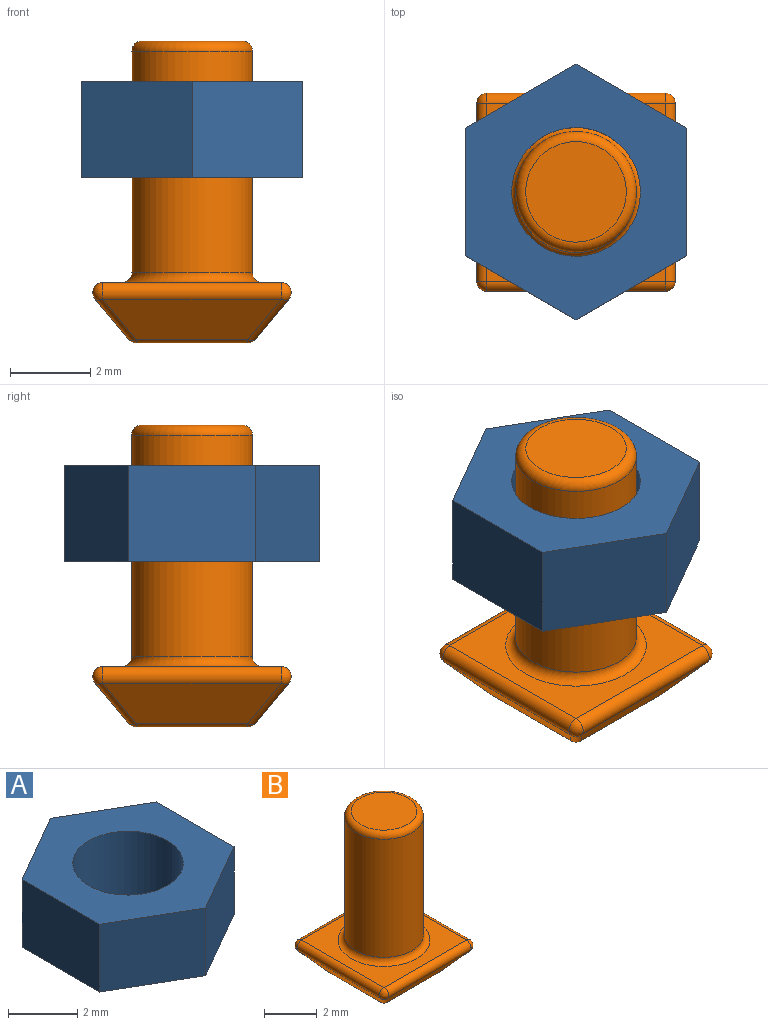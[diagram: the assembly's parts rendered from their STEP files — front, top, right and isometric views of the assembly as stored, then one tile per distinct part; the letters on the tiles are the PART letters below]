
ASSEMBLY  parts=2 mates=2
PART A: 9 faces, bbox 5.5x6.4x2.4 mm
  f0: plane 3.18x2.4mm, normal (1,0,0), area 7.6mm2, adj f1,f5,f7,f8
  f1: plane 2.75x2.4mm, normal (0.5,0.87,0), area 7.6mm2, adj f0,f2,f7,f8
  f2: plane 2.75x2.4mm, normal (-0.5,0.87,0), area 7.6mm2, adj f1,f3,f7,f8
  f3: plane 3.18x2.4mm, normal (-1,0,0), area 7.6mm2, adj f2,f4,f7,f8
  f4: plane 2.75x2.4mm, normal (-0.5,-0.87,0), area 7.6mm2, adj f3,f5,f7,f8
  f5: plane 2.75x2.4mm, normal (0.5,-0.87,0), area 7.6mm2, adj f0,f4,f7,f8
  f6: cylinder r=1.6mm len=3.2mm, axis (0,0,-1), area 24.1mm2, adj f7,f8
  f7: plane 6.35x5.5mm, normal (0,0,1), area 18.2mm2, adj f0,f1,f2,f3,f4,f5,f6
  f8: plane 6.35x5.5mm, normal (0,0,-1), area 18.2mm2, adj f0,f1,f2,f3,f4,f5,f6
PART B: 37 faces, bbox 4.9x4.9x7.5 mm
  f0: plane 2.77x2.77mm, normal (0,0,-1), area 4.2mm2, adj f6,f7,f8,f9,f10,f11,f20,f21
  f1: plane 4.43x1mm, normal (0,0.77,-0.64), area 4.7mm2, adj f25,f30,f33,f36
  f2: plane 4.43x1mm, normal (0,-0.77,-0.64), area 4.7mm2, adj f17,f21,f22,f23
  f3: plane 4.43x4.43mm, normal (0,0,1), area 10mm2, adj f15,f23,f24,f32,f33
  f4: plane 4.43x1mm, normal (-0.77,0,-0.64), area 4.7mm2, adj f17,f20,f24,f25
  f5: plane 4.43x1mm, normal (0.77,0,-0.64), area 4.7mm2, adj f22,f31,f32,f36
  f6: plane 1x1mm, normal (-0.5,0.87,0), area 1.2mm2, adj f0,f7,f11,f12
  f7: plane 1x1mm, normal (0.5,0.87,0), area 1.2mm2, adj f0,f6,f8,f12
  f8: plane 1.15x1mm, normal (1,0,0), area 1.2mm2, adj f0,f7,f9,f12
  f9: plane 1x1mm, normal (0.5,-0.87,0), area 1.2mm2, adj f0,f8,f10,f12
  f10: plane 1x1mm, normal (-0.5,-0.87,0), area 1.2mm2, adj f0,f9,f11,f12
  f11: plane 1.15x1mm, normal (-1,0,0), area 1.2mm2, adj f0,f6,f10,f12
  f12: plane 2.31x2mm, normal (0,0,-1), area 3.5mm2, adj f6,f7,f8,f9,f10,f11
  f13: cylinder r=1.5mm len=5.5mm, axis (0,0,-1), area 51.8mm2, adj f15,f16
  f14: plane 2.5x2.5mm, normal (0,0,1), area 4.9mm2, adj f16
  f15: torus R=1.75mm, axis (0,0,1), area 3.9mm2, adj f3,f13
  f16: torus R=1.25mm, axis (0,0,1), area 3.5mm2, adj f13,f14
  f17: cylinder r=0.25mm len=1.03mm, axis (0.54,0.54,-0.65), area 0.4mm2, adj f2,f4,f18,f19
  f18: sphere r=0.25mm, area 0mm2, adj f17,f20,f21
  f19: sphere r=0.25mm, area 0.2mm2, adj f17,f23,f24
  f20: cylinder r=0.25mm len=2.77mm, axis (0,-1,0), area 0.6mm2, adj f0,f4,f18,f26
  f21: cylinder r=0.25mm len=2.77mm, axis (1,0,0), area 0.6mm2, adj f0,f2,f18,f27
  f22: cylinder r=0.25mm len=1.03mm, axis (0.54,-0.54,0.65), area 0.4mm2, adj f2,f5,f27,f28
  f23: cylinder r=0.25mm len=4.43mm, axis (1,0,0), area 2.5mm2, adj f2,f3,f19,f28
  f24: cylinder r=0.25mm len=4.43mm, axis (0,-1,0), area 2.5mm2, adj f3,f4,f19,f29
  f25: cylinder r=0.25mm len=1.03mm, axis (-0.54,0.54,0.65), area 0.4mm2, adj f1,f4,f26,f29
  f26: sphere r=0.25mm, area 0mm2, adj f20,f25,f30
  f27: sphere r=0.25mm, area 0mm2, adj f21,f22,f31
  f28: sphere r=0.25mm, area 0.2mm2, adj f22,f23,f32
  f29: sphere r=0.25mm, area 0.2mm2, adj f24,f25,f33
  f30: cylinder r=0.25mm len=2.77mm, axis (-1,0,0), area 0.6mm2, adj f0,f1,f26,f34
  f31: cylinder r=0.25mm len=2.77mm, axis (0,1,0), area 0.6mm2, adj f0,f5,f27,f34
  f32: cylinder r=0.25mm len=4.43mm, axis (0,1,0), area 2.5mm2, adj f3,f5,f28,f35
  f33: cylinder r=0.25mm len=4.43mm, axis (-1,0,0), area 2.5mm2, adj f1,f3,f29,f35
  f34: sphere r=0.25mm, area 0mm2, adj f30,f31,f36
  f35: sphere r=0.25mm, area 0.2mm2, adj f32,f33,f36
  f36: cylinder r=0.25mm len=1.03mm, axis (-0.54,-0.54,-0.65), area 0.4mm2, adj f1,f5,f34,f35
PLACE A t=(-3.68,-0.97,-1.72)mm
PLACE B t=(-3.68,-0.97,-4.32)mm
MATE planar A.f8 <-> B.f13  axis (0,0,-1) through (-3.68,-4.15,-1.72)mm
MATE cylindrical A.f6 <-> B.f13  axis (0,0,1) through (-3.68,-0.97,0.68)mm
